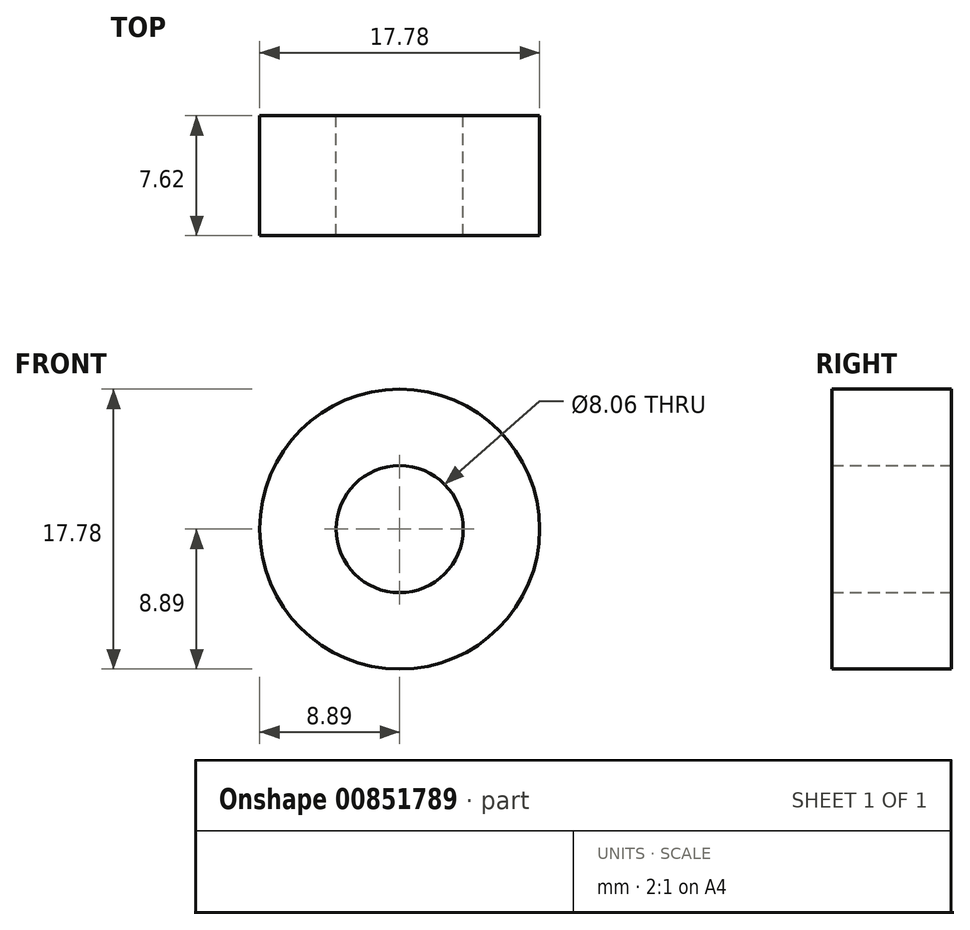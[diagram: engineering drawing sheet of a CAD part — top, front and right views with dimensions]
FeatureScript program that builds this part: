
annotation { "Feature Type Name" : "Feature", "Feature Type Description" : "" }
export const myFeature = defineFeature(function(context is Context, id is Id, definition is map)
    precondition{}
    {
        {
            var Q0;
            Q0=qCreatedBy(makeId("Front.planeOp"),FACE);
            var sketch = newSketch(context, id + "F0", { "sketchPlane" : qUnion([Q0])});
            skCircle(sketch, "E0", {"center": v(0, 0) * mm, "radius": 4.03 * mm});
            skCircle(sketch, "E1", {"center": v(0, 0) * mm, "radius": 8.9 * mm});
            skSolve(sketch);
        }
        {
            var Q0;
            Q0=makeQuery(id+"F0.imprint","IMPRINT",FACE,{"disambiguationData":[TD([[makeQuery(id+"F0.imprint","IMPRINT",EDGE,{"derivedFrom":sQuery(id+"F0.wireOp",EDGE,"E0")}),-1.0]])]});
            extrude(context, id + "F1", {"entities" : qUnion([Q0]), "depth" : 7.62 * mm, "offsetDistance" : 25.4 * mm});
        }
    });
